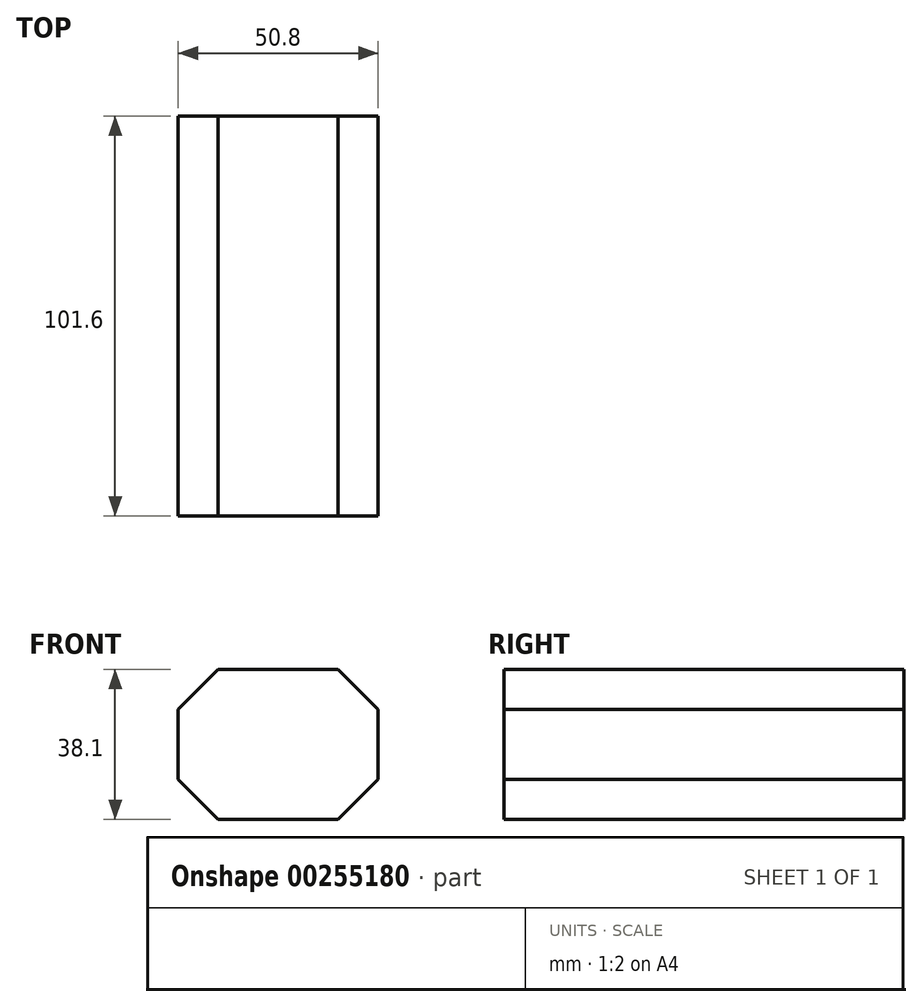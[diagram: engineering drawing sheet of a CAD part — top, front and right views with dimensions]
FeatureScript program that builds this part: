
annotation { "Feature Type Name" : "Feature", "Feature Type Description" : "" }
export const myFeature = defineFeature(function(context is Context, id is Id, definition is map)
    precondition{}
    {
        {
            var Q0;
            Q0=qCreatedBy(makeId("Front.planeOp"),FACE);
            var sketch = newSketch(context, id + "F0", { "sketchPlane" : qUnion([Q0])});
            skLineSegment(sketch, "E0.rect.bottom", {"start": v(-25.4, 19.05) * mm, "end": v(25.4, 19.05) * mm});
            skLineSegment(sketch, "E0.rect.top", {"start": v(-25.4, -19.05) * mm, "end": v(25.4, -19.05) * mm});
            skLineSegment(sketch, "E0.rect.left", {"start": v(-25.4, 19.05) * mm, "end": v(-25.4, -19.05) * mm});
            skLineSegment(sketch, "E0.rect.right", {"start": v(25.4, 19.05) * mm, "end": v(25.4, -19.05) * mm});
            skPoint(sketch, "E0.rect.middle", {"position": v(0, 0) * mm});
            skSolve(sketch);
        }
        {
            var Q0;
            Q0=qSketchRegion(id+"F0",true);
            extrude(context, id + "F1", {"entities" : qUnion([Q0]), "depth" : 101.6 * mm});
        }
        {
            var Q0;
            Q0=makeQuery(id+"F1.opExtrude","SWEPT_EDGE",EDGE,{"disambiguationData":[OSD([sQuery(id+"F0.wireOp",EDGE,"E0.rect.bottom"),sQuery(id+"F0.wireOp",EDGE,"E0.rect.left")])]});
            var Q1;
            Q1=makeQuery(id+"F1.opExtrude","SWEPT_EDGE",EDGE,{"disambiguationData":[OSD([sQuery(id+"F0.wireOp",EDGE,"E0.rect.top"),sQuery(id+"F0.wireOp",EDGE,"E0.rect.left")])]});
            var Q2;
            Q2=makeQuery(id+"F1.opExtrude","SWEPT_EDGE",EDGE,{"disambiguationData":[OSD([sQuery(id+"F0.wireOp",EDGE,"E0.rect.top"),sQuery(id+"F0.wireOp",EDGE,"E0.rect.right")])]});
            var Q3;
            Q3=makeQuery(id+"F1.opExtrude","SWEPT_EDGE",EDGE,{"disambiguationData":[OSD([sQuery(id+"F0.wireOp",EDGE,"E0.rect.bottom"),sQuery(id+"F0.wireOp",EDGE,"E0.rect.right")])]});
            chamfer(context, id + "F2", {"entities" : qUnion([Q0, Q1, Q2, Q3]), "width" : 10.16 * mm, "tangentPropagation" : true});
        }
    });
